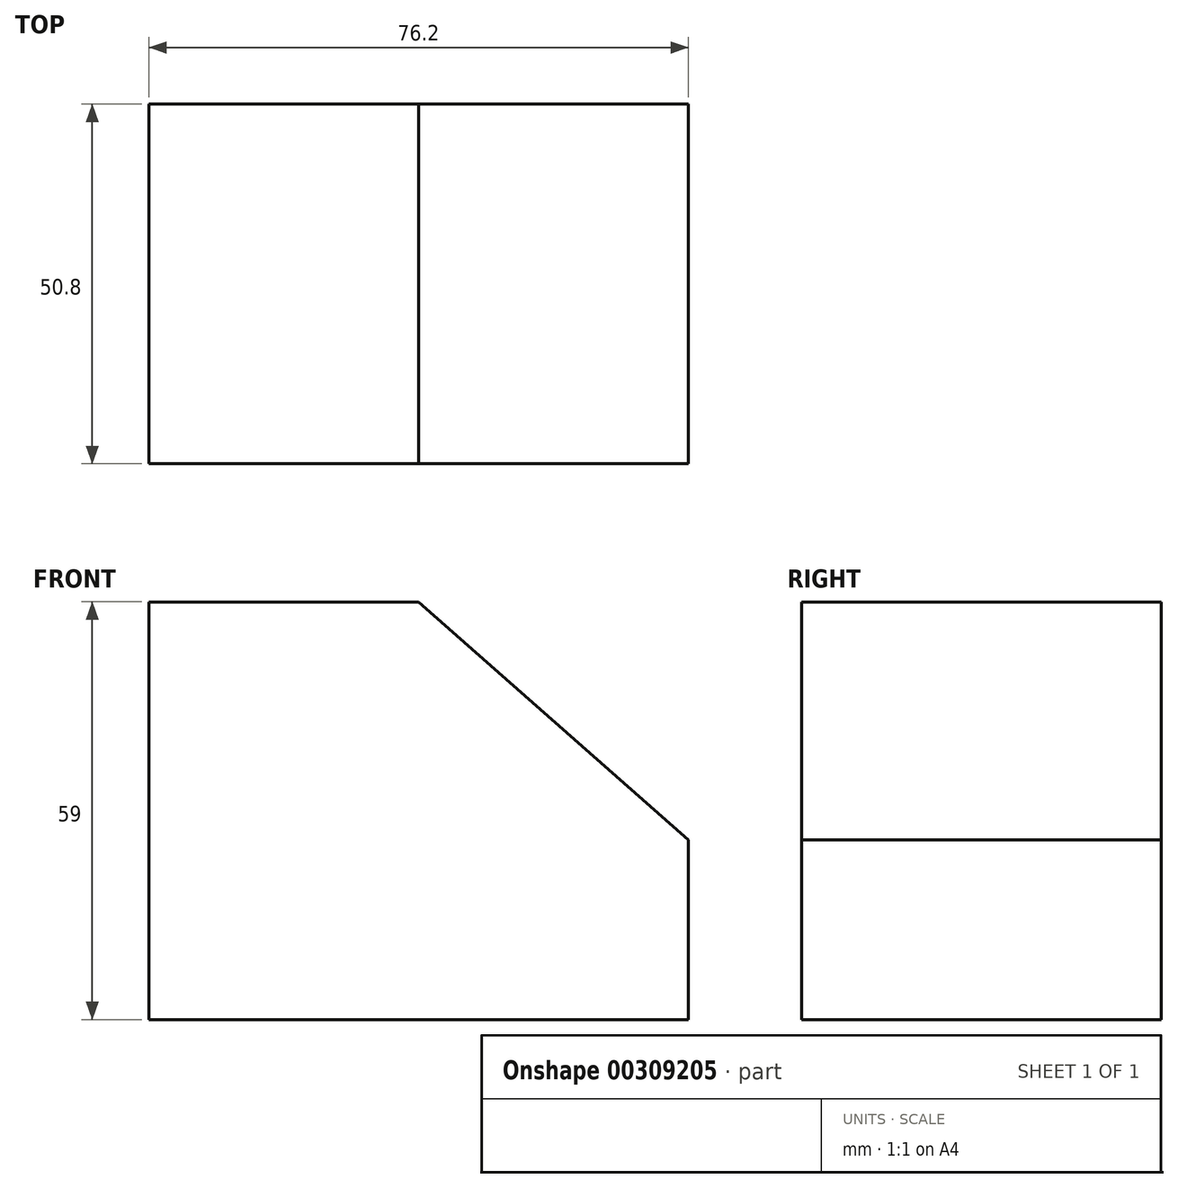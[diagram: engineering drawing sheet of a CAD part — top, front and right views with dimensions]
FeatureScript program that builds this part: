
annotation { "Feature Type Name" : "Feature", "Feature Type Description" : "" }
export const myFeature = defineFeature(function(context is Context, id is Id, definition is map)
    precondition{}
    {
        {
            var Q0;
            Q0=qCreatedBy(makeId("Front.planeOp"),FACE);
            var sketch = newSketch(context, id + "F0", { "sketchPlane" : qUnion([Q0])});
            skLineSegment(sketch, "E0", {"start": v(-48.82, -29.4) * mm, "end": v(27.38, -29.4) * mm});
            skLineSegment(sketch, "E1", {"start": v(27.38, -29.4) * mm, "end": v(27.38, -4) * mm});
            skLineSegment(sketch, "E2", {"start": v(27.38, -4) * mm, "end": v(-10.72, 29.6) * mm});
            skLineSegment(sketch, "E3", {"start": v(-10.72, 29.6) * mm, "end": v(-48.82, 29.6) * mm});
            skLineSegment(sketch, "E4", {"start": v(-48.82, 29.6) * mm, "end": v(-48.82, -29.4) * mm});
            skSolve(sketch);
        }
        {
            var Q0;
            Q0=makeQuery(id+"F0.imprint","IMPRINT",FACE,{"disambiguationData":[TD([[makeQuery(id+"F0.imprint","IMPRINT",EDGE,{"derivedFrom":sQuery(id+"F0.wireOp",EDGE,"E0")}),1.0]])]});
            extrude(context, id + "F1", {"entities" : qUnion([Q0]), "depth" : 50.8 * mm});
        }
    });
